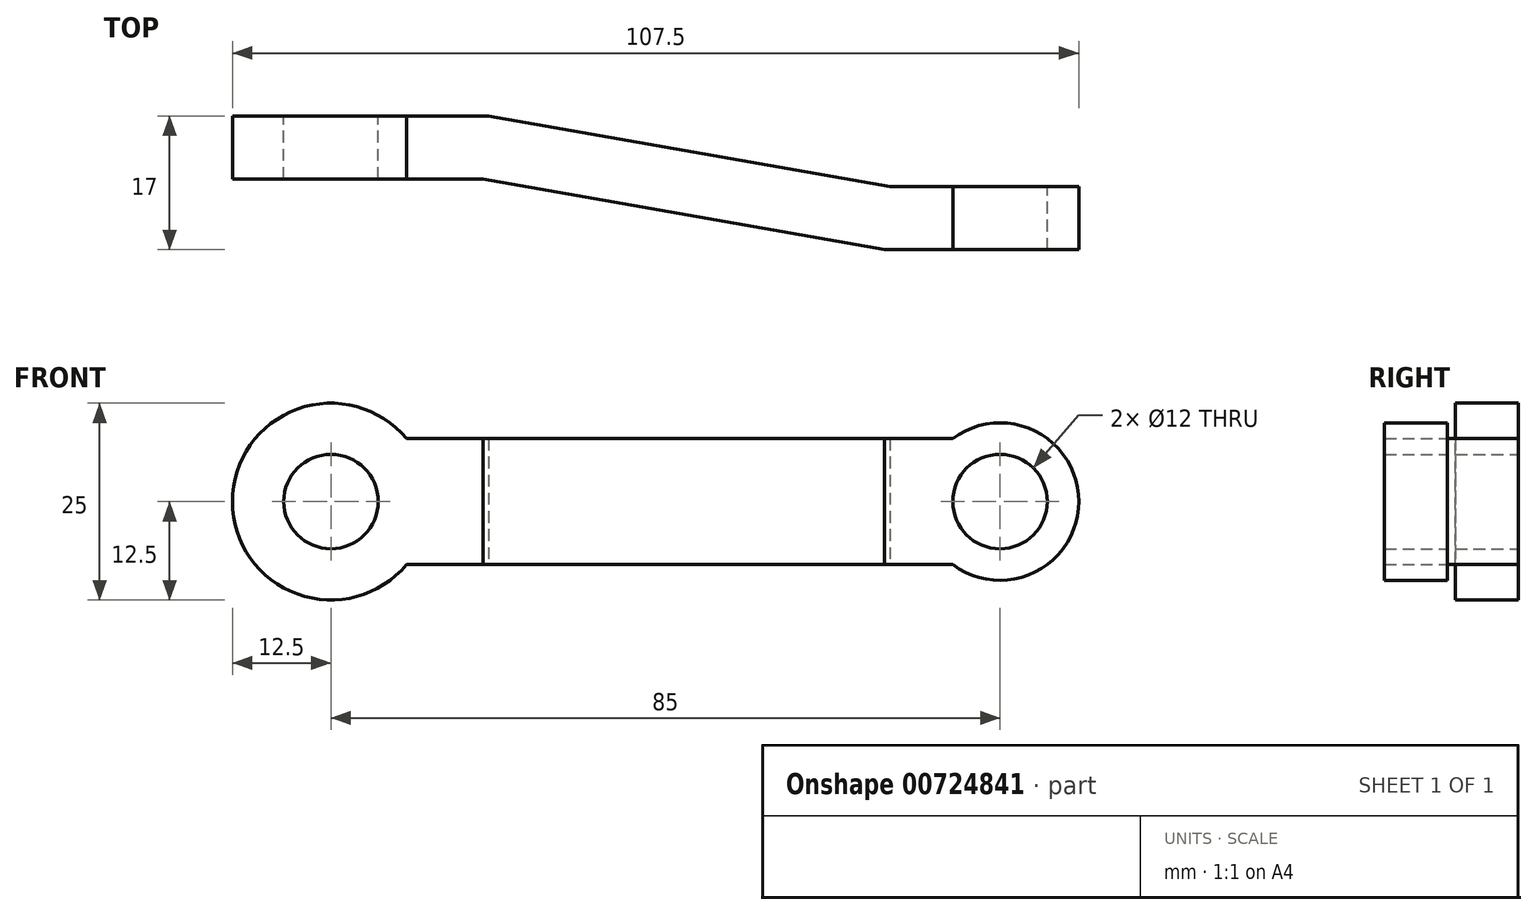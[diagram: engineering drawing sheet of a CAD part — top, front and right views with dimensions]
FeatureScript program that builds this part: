
annotation { "Feature Type Name" : "Feature", "Feature Type Description" : "" }
export const myFeature = defineFeature(function(context is Context, id is Id, definition is map)
    precondition{}
    {
        {
            var Q0;
            Q0=qCreatedBy(makeId("Front.planeOp"),FACE);
            var sketch = newSketch(context, id + "F0", { "sketchPlane" : qUnion([Q0])});
            skCircle(sketch, "E0", {"center": v(0, 0) * mm, "radius": 12.5 * mm});
            skCircle(sketch, "E1", {"center": v(85, 0) * mm, "radius": 10 * mm});
            skLineSegment(sketch, "E2", {"start": v(0, 0) * mm, "end": v(85, 0) * mm, "construction": true});
            skLineSegment(sketch, "E3", {"start": v(9.6, 8) * mm, "end": v(79, 8) * mm});
            skLineSegment(sketch, "E4.MirrorCS", {"start": v(9.6, -8) * mm, "end": v(79, -8) * mm});
            skCircle(sketch, "E5", {"center": v(0, 0) * mm, "radius": 6 * mm});
            skCircle(sketch, "E6", {"center": v(85, 0) * mm, "radius": 6 * mm});
            skSolve(sketch);
        }
        {
            var Q0;
            Q0 = qSketchRegion(id + "F0", true);
            extrude(context, id + "F1", {"entities" : qUnion([Q0]), "depth" : 25 * mm, "offsetDistance" : 25.4 * mm});
        }
        {
            var Q0;
            Q0=qCreatedBy(makeId("Top.planeOp"),FACE);
            var sketch = newSketch(context, id + "F2", { "sketchPlane" : qUnion([Q0])});
            skLineSegment(sketch, "E7", {"start": v(-12.5, 0) * mm, "end": v(20, 0) * mm});
            skLineSegment(sketch, "E8", {"start": v(20, 0) * mm, "end": v(71.04, -9) * mm});
            skLineSegment(sketch, "E9", {"start": v(71.04, -9) * mm, "end": v(95, -9) * mm});
            skLineSegment(sketch, "E10.0", {"start": v(70.34, -17) * mm, "end": v(95, -17) * mm});
            skLineSegment(sketch, "E10.1", {"start": v(19.3, -8) * mm, "end": v(70.34, -17) * mm});
            skLineSegment(sketch, "E10.2", {"start": v(-12.5, -8) * mm, "end": v(19.3, -8) * mm});
            skLineSegment(sketch, "E11", {"start": v(95, -9) * mm, "end": v(95, -17) * mm});
            skLineSegment(sketch, "E12", {"start": v(-12.5, 0) * mm, "end": v(-12.5, -8) * mm});
            skLineSegment(sketch, "E13", {"start": v(95, 0) * mm, "end": v(95, -25) * mm});
            skLineSegment(sketch, "E14", {"start": v(-12.5, -25) * mm, "end": v(-12.5, 0) * mm});
            skSolve(sketch);
        }
        {
            var Q0;
            Q0 = qSketchRegion(id + "F2", true);
            extrude(context, id + "F3", {"entities" : qUnion([Q0]), "operationType" : NewBodyOperationType.INTERSECT, "endBound" : BoundingType.SYMMETRIC, "depth" : 25.4 * mm, "offsetDistance" : 25.4 * mm});
        }
    });
